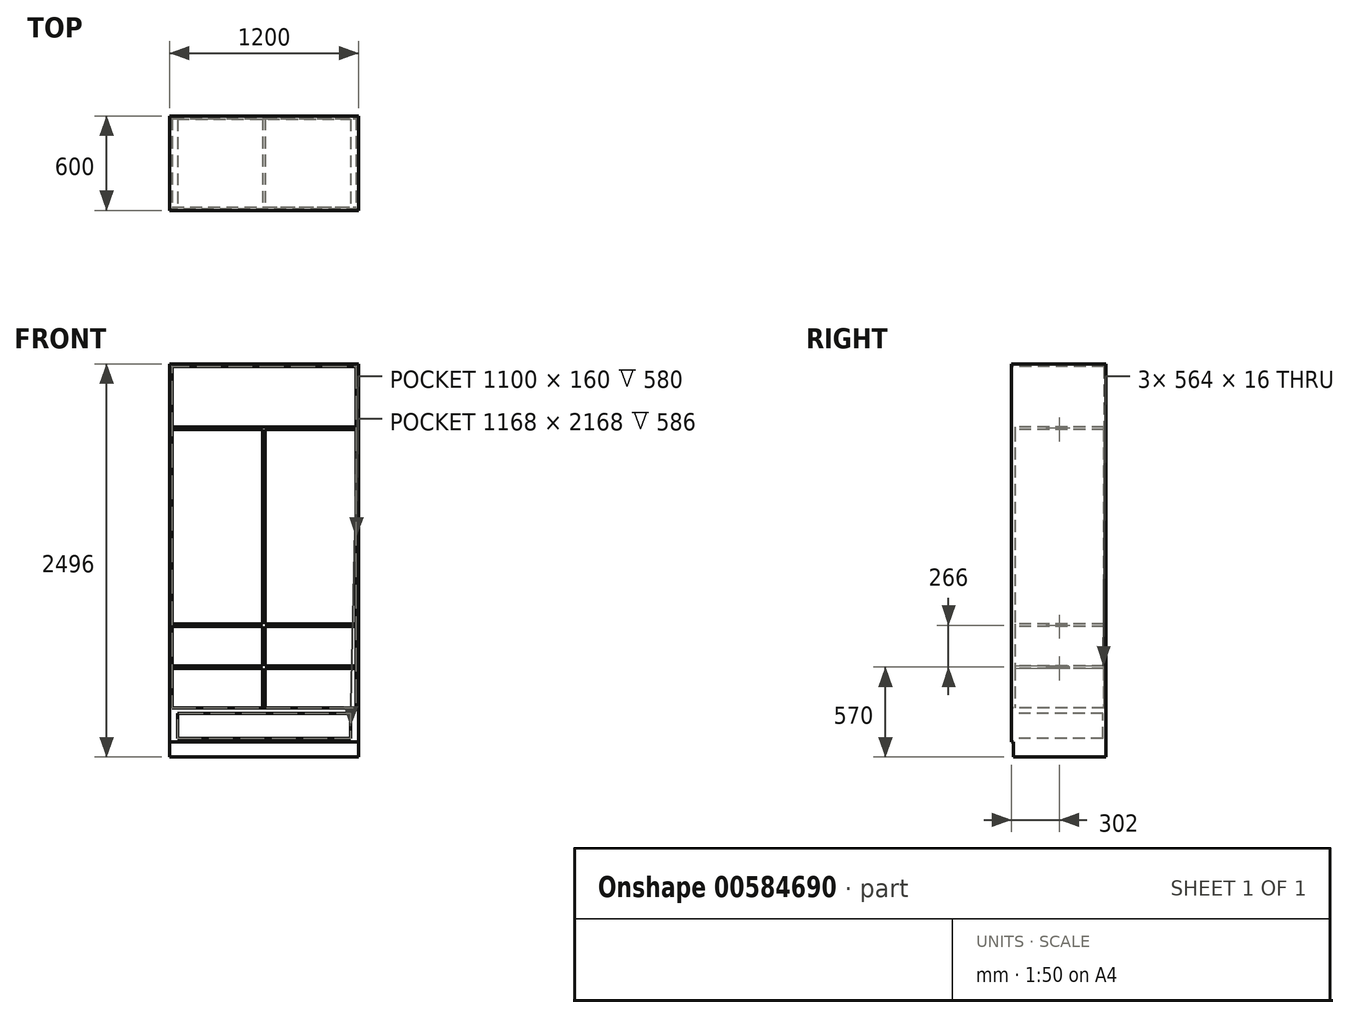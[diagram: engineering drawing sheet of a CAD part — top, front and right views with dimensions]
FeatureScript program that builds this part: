
annotation { "Feature Type Name" : "Feature", "Feature Type Description" : "" }
export const myFeature = defineFeature(function(context is Context, id is Id, definition is map)
    precondition{}
    {
        {
            var Q0;
            Q0=qCreatedBy(makeId("Right.planeOp"),FACE);
            var sketch = newSketch(context, id + "F0", { "sketchPlane" : qUnion([Q0])});
            skLineSegment(sketch, "E0.bottom", {"start": v(300, -1248) * mm, "end": v(-300, -1248) * mm});
            skLineSegment(sketch, "E0.top", {"start": v(300, 1248) * mm, "end": v(-300, 1248) * mm});
            skLineSegment(sketch, "E0.left", {"start": v(300, -1248) * mm, "end": v(300, 1248) * mm});
            skLineSegment(sketch, "E0.right", {"start": v(-300, -1248) * mm, "end": v(-300, 1248) * mm});
            skPoint(sketch, "E0.middle", {"position": v(0, 0) * mm});
            skSolve(sketch);
        }
        {
            var Q0;
            Q0=qSketchRegion(id+"F0",true);
            extrude(context, id + "F1", {"entities" : qUnion([Q0]), "depth" : 1200 * mm, "offsetDistance" : 25 * mm});
        }
        {
            var Q0;
            Q0=makeQuery(id+"F1.opExtrude","SWEPT_FACE",FACE,{"disambiguationData":[OSD([sQuery(id+"F0.wireOp",EDGE,"E0.right")])]});
            var sketch = newSketch(context, id + "F2", { "sketchPlane" : qUnion([Q0])});
            skLineSegment(sketch, "E1.bottom", {"start": v(0, -1248) * mm, "end": v(1200, -1248) * mm});
            skLineSegment(sketch, "E1.top", {"start": v(0, -1152) * mm, "end": v(1200, -1152) * mm});
            skLineSegment(sketch, "E1.left", {"start": v(0, -1248) * mm, "end": v(0, -1152) * mm});
            skLineSegment(sketch, "E1.right", {"start": v(1200, -1248) * mm, "end": v(1200, -1152) * mm});
            skSolve(sketch);
        }
        {
            var Q0;
            Q0=qSketchRegion(id+"F2",true);
            extrude(context, id + "F3", {"entities" : qUnion([Q0]), "operationType" : NewBodyOperationType.REMOVE, "oppositeDirection" : true, "depth" : 10 * mm, "offsetDistance" : 25 * mm});
        }
        {
            var Q0;
            Q0=makeQuery(id+"F1.opExtrude","SWEPT_FACE",FACE,{"disambiguationData":[OSD([sQuery(id+"F0.wireOp",EDGE,"E0.right")])]});
            var sketch = newSketch(context, id + "F4", { "sketchPlane" : qUnion([Q0])});
            skLineSegment(sketch, "E2.bottom", {"start": v(0, -1152) * mm, "end": v(1200, -1152) * mm});
            skLineSegment(sketch, "E2.top", {"start": v(0, -952) * mm, "end": v(1200, -952) * mm});
            skLineSegment(sketch, "E2.left", {"start": v(0, -1152) * mm, "end": v(0, -952) * mm});
            skLineSegment(sketch, "E2.right", {"start": v(1200, -1152) * mm, "end": v(1200, -952) * mm});
            skLineSegment(sketch, "E3.bottom", {"start": v(50, -1132) * mm, "end": v(1150, -1132) * mm});
            skLineSegment(sketch, "E3.top", {"start": v(50, -972) * mm, "end": v(1150, -972) * mm});
            skLineSegment(sketch, "E3.left", {"start": v(50, -1132) * mm, "end": v(50, -972) * mm});
            skLineSegment(sketch, "E3.right", {"start": v(1150, -1132) * mm, "end": v(1150, -972) * mm});
            skSolve(sketch);
        }
        {
            var Q0;
            Q0=makeQuery(id+"F4.imprint","IMPRINT",FACE,{"disambiguationData":[TD([[makeQuery(id+"F4.imprint","IMPRINT",EDGE,{"derivedFrom":sQuery(id+"F4.wireOp",EDGE,"E3.bottom")}),1.0]])]});
            extrude(context, id + "F5", {"entities" : qUnion([Q0]), "operationType" : NewBodyOperationType.REMOVE, "oppositeDirection" : true, "depth" : 580 * mm, "offsetDistance" : 25 * mm});
        }
        {
            var Q0;
            {var subQ0=sQuery(id+"F4.wireOp",EDGE,"E2.top");Q0=makeQuery(id+"F4.imprint","IMPRINT",FACE,{"disambiguationData":[TD([[makeQuery(id+"F4.imprint","IMPRINT",EDGE,{"derivedFrom":subQ0}),1.0]])]});}
            cPlane(context, id + "F6", {"entities" : qUnion([Q0]), "cplaneType" : CPlaneType.OFFSET, "offset" : 20 * mm, "oppositeDirection" : true, "width" : 150 * mm, "height" : 150 * mm});
        }
        {
            var Q0;
            {var subQ0=sQuery(id+"F4.wireOp",EDGE,"E2.top");Q0=makeQuery(id+"F4.imprint","IMPRINT",FACE,{"disambiguationData":[TD([[makeQuery(id+"F4.imprint","IMPRINT",EDGE,{"derivedFrom":subQ0}),1.0]])]});}
            var sketch = newSketch(context, id + "F7", { "sketchPlane" : qUnion([Q0])});
            skLineSegment(sketch, "E4.bottom", {"start": v(16, 1232) * mm, "end": v(1184, 1232) * mm});
            skLineSegment(sketch, "E4.top", {"start": v(16, -936) * mm, "end": v(1184, -936) * mm});
            skLineSegment(sketch, "E4.left", {"start": v(16, 1232) * mm, "end": v(16, -936) * mm});
            skLineSegment(sketch, "E4.right", {"start": v(1184, 1232) * mm, "end": v(1184, -936) * mm});
            skSolve(sketch);
        }
        {
            var Q0;
            Q0 = qSketchRegion(id + "F7", true);
            extrude(context, id + "F8", {"entities" : qUnion([Q0]), "operationType" : NewBodyOperationType.REMOVE, "oppositeDirection" : true, "depth" : 586 * mm, "offsetDistance" : 25 * mm});
        }
        {
            var Q0;
            Q0=qCreatedBy(id+"F6.planeOp",FACE);
            var sketch = newSketch(context, id + "F9", { "sketchPlane" : qUnion([Q0])});
            skLineSegment(sketch, "E5.bottom", {"start": v(16, 848) * mm, "end": v(1184, 848) * mm});
            skLineSegment(sketch, "E5.top", {"start": v(16, 832) * mm, "end": v(1184, 832) * mm});
            skLineSegment(sketch, "E5.left", {"start": v(16, 848) * mm, "end": v(16, 832) * mm});
            skLineSegment(sketch, "E5.right", {"start": v(1184, 848) * mm, "end": v(1184, 832) * mm});
            skSolve(sketch);
        }
        {
            var Q0;
            Q0 = qSketchRegion(id + "F9", true);
            extrude(context, id + "F10", {"entities" : qUnion([Q0]), "operationType" : NewBodyOperationType.ADD, "oppositeDirection" : true, "depth" : 564 * mm, "offsetDistance" : 25 * mm});
        }
        {
            var Q0;
            Q0=qCreatedBy(id+"F6.planeOp",FACE);
            var sketch = newSketch(context, id + "F11", { "sketchPlane" : qUnion([Q0])});
            skLineSegment(sketch, "E6.bottom", {"start": v(592, 832) * mm, "end": v(608, 832) * mm});
            skLineSegment(sketch, "E6.top", {"start": v(592, -936) * mm, "end": v(608, -936) * mm});
            skLineSegment(sketch, "E6.left", {"start": v(592, 832) * mm, "end": v(592, -936) * mm});
            skLineSegment(sketch, "E6.right", {"start": v(608, 832) * mm, "end": v(608, -936) * mm});
            skSolve(sketch);
        }
        {
            var Q0;
            Q0 = qSketchRegion(id + "F11", true);
            var Q1;
            Q1=sQuery(id+"F11.wireOp",EDGE,"E6.left");
            extrude(context, id + "F12", {"entities" : qUnion([Q0]), "operationType" : NewBodyOperationType.ADD, "surfaceEntities" : qUnion([Q1]), "oppositeDirection" : true, "depth" : 564 * mm, "offsetDistance" : 25 * mm});
        }
        {
            var Q0;
            Q0=qCreatedBy(id+"F6.planeOp",FACE);
            var sketch = newSketch(context, id + "F13", { "sketchPlane" : qUnion([Q0])});
            skLineSegment(sketch, "E7.bottom", {"start": v(16, -670) * mm, "end": v(1184, -670) * mm});
            skLineSegment(sketch, "E7.top", {"start": v(16, -686) * mm, "end": v(1184, -686) * mm});
            skLineSegment(sketch, "E7.left", {"start": v(16, -670) * mm, "end": v(16, -686) * mm});
            skLineSegment(sketch, "E7.right", {"start": v(1184, -670) * mm, "end": v(1184, -686) * mm});
            skLineSegment(sketch, "E8.bottom", {"start": v(16, -404) * mm, "end": v(1184, -404) * mm});
            skLineSegment(sketch, "E8.top", {"start": v(16, -420) * mm, "end": v(1184, -420) * mm});
            skLineSegment(sketch, "E8.left", {"start": v(16, -404) * mm, "end": v(16, -420) * mm});
            skLineSegment(sketch, "E8.right", {"start": v(1184, -404) * mm, "end": v(1184, -420) * mm});
            skSolve(sketch);
        }
        {
            var Q0;
            Q0 = qSketchRegion(id + "F13", true);
            extrude(context, id + "F14", {"entities" : qUnion([Q0]), "operationType" : NewBodyOperationType.ADD, "oppositeDirection" : true, "depth" : 564 * mm, "offsetDistance" : 25 * mm});
        }
    });
